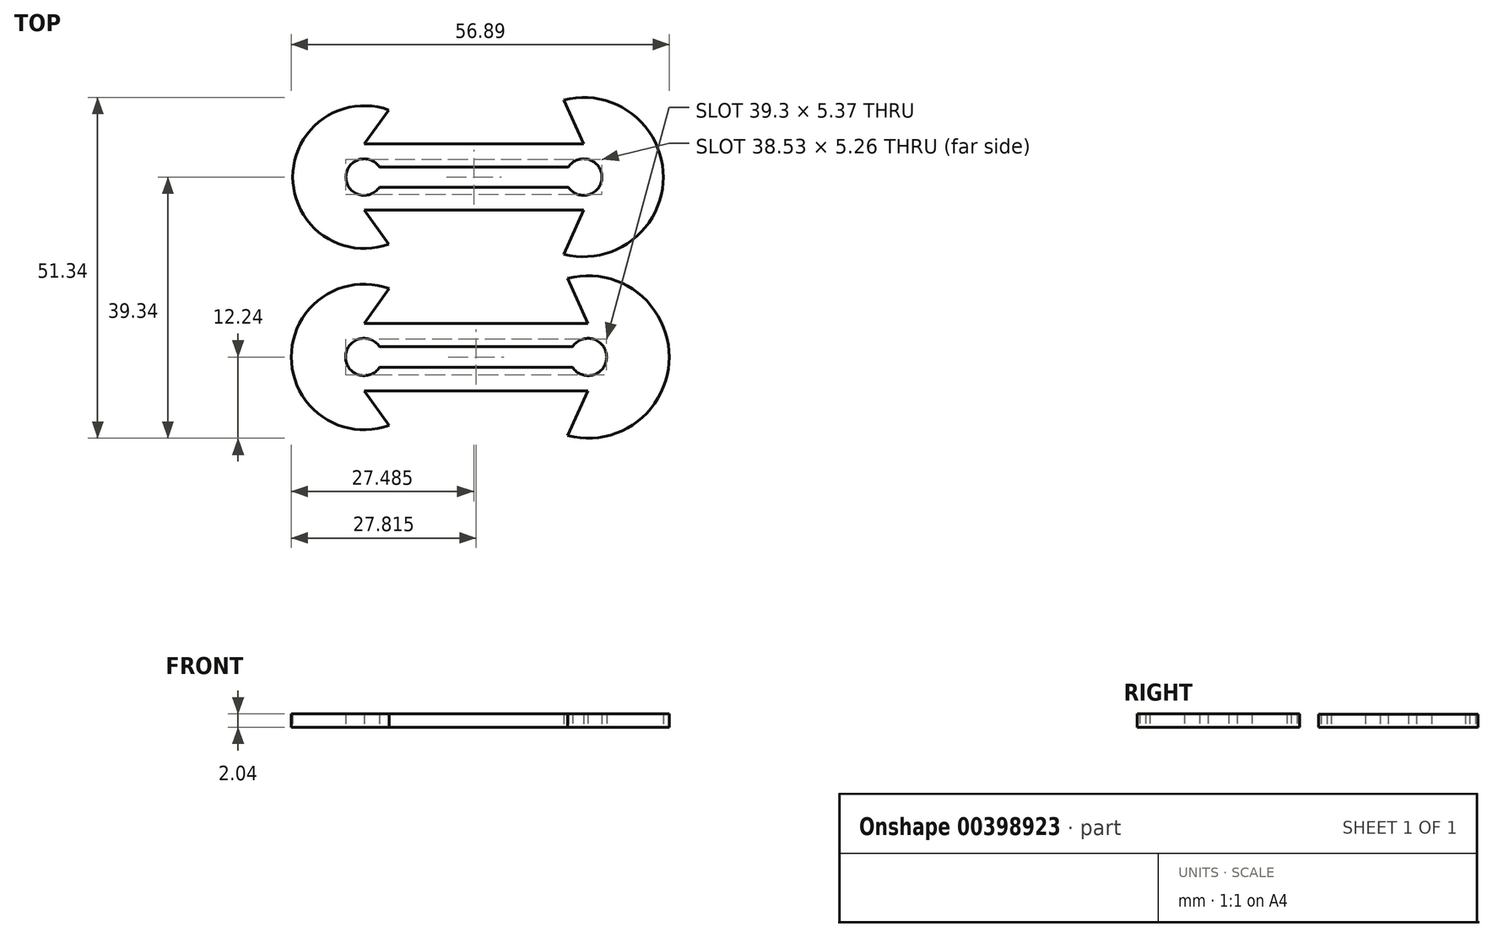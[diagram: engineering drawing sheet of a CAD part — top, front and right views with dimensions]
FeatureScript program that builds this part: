
annotation { "Feature Type Name" : "Feature", "Feature Type Description" : "" }
export const myFeature = defineFeature(function(context is Context, id is Id, definition is map)
    precondition{}
    {
        {
            var Q0;
            Q0=qCreatedBy(makeId("Top.planeOp"),FACE);
            var sketch = newSketch(context, id + "F0", { "sketchPlane" : qUnion([Q0])});
            skArc(sketch, "E0", {"start": v(3.68, 10.1) * mm, "mid": v(-10.75, 0) * mm, "end": v(3.68, -10.1) * mm});
            skArc(sketch, "E1", {"start": v(30.04, -11.62) * mm, "mid": v(45.02, 0) * mm, "end": v(30.04, 11.62) * mm});
            skPoint(sketch, "E2.orphan", {"position": v(0, 4.36) * mm});
            skLineSegment(sketch, "E3.top", {"start": v(0, 4.98) * mm, "end": v(33.02, 4.98) * mm});
            skPoint(sketch, "E4.orphan", {"position": v(0, 10.75) * mm});
            skLineSegment(sketch, "E5", {"start": v(3.68, 10.1) * mm, "end": v(0, 4.98) * mm});
            skLineSegment(sketch, "E6", {"start": v(3.68, -10.1) * mm, "end": v(0, -4.98) * mm});
            skPoint(sketch, "E7.orphan", {"position": v(30.04, -11.62) * mm});
            skLineSegment(sketch, "E8", {"start": v(30.04, 11.62) * mm, "end": v(33.02, 4.98) * mm});
            skLineSegment(sketch, "E9", {"start": v(30.04, -11.62) * mm, "end": v(33.02, -4.98) * mm});
            skPoint(sketch, "E10.orphan", {"position": v(33.02, 12) * mm});
            skLineSegment(sketch, "E11.bottom", {"start": v(0, 0) * mm, "end": v(33.03, 0) * mm});
            skLineSegment(sketch, "E11.top", {"start": v(0, -1.54) * mm, "end": v(33.03, -1.54) * mm});
            skLineSegment(sketch, "E11.left", {"start": v(0, 0) * mm, "end": v(0, -1.54) * mm});
            skLineSegment(sketch, "E11.right", {"start": v(33.03, 0) * mm, "end": v(33.03, -1.54) * mm});
            skLineSegment(sketch, "E12.MirrorCS", {"start": v(0, 1.54) * mm, "end": v(33.03, 1.54) * mm});
            skLineSegment(sketch, "E13.MirrorCS", {"start": v(0, 0) * mm, "end": v(0, 1.54) * mm});
            skLineSegment(sketch, "E14.MirrorCS", {"start": v(33.03, 0) * mm, "end": v(33.03, 1.54) * mm});
            skLineSegment(sketch, "E15.MirrorCS", {"start": v(0, -4.98) * mm, "end": v(33.02, -4.98) * mm});
            skSolve(sketch);
        }
        {
            var Q0;
            Q0=qSketchRegion(id+"F0",true);
            extrude(context, id + "F1", {"entities" : qUnion([Q0]), "depth" : 2 * mm});
        }
        {
            var Q0;
            Q0=sQuery(id+"F0.wireOp",VERTEX,"E11.bottom.start");
            var Q1;
            Q1=sQuery(id+"F0.wireOp",VERTEX,"E11.right.start");
            var Q2;
            Q2=makeQuery(id+"F1.opExtrude","SWEPT_BODY",BODY,{"disambiguationData":[OSD([sQuery(id+"F0.wireOp",EDGE,"E0"),sQuery(id+"F0.wireOp",EDGE,"E1"),sQuery(id+"F0.wireOp",EDGE,"E3.top"),sQuery(id+"F0.wireOp",EDGE,"09a4da2d-7d0f-4de4-b051-a0dd602dcae70.MirrorCS"),sQuery(id+"F0.wireOp",EDGE,"kJXo7HvB-q0wJ-KMkF-qbSK-HqD1jnp9HCBe"),sQuery(id+"F0.wireOp",EDGE,"2FfrFlms-cFN7-iBXT-GTBb-5V8th5hE76g1")])]});
            hole(context, id + "F2", {"style" : HoleStyle.SIMPLE, "endStyle" : HoleEndStyle.THROUGH, "oppositeDirection" : true, "standardTappedOrClearance" : lookupTablePath({ "standard" : "ISO", "fit" : "Normal", "size" : "M5", "type" : "Clearance" }), "standardBlindInLast" : lookupTablePath({ "fit" : "Standard", "standard" : "ISO", "size" : "M5", "type" : "Clearance" }), "holeDiameter" : 5.5 * mm, "isTappedThrough" : true, "tappedDepth" : 12 * mm, "tapClearance" : 3, "locations" : qUnion([Q0, Q1]), "scope" : qUnion([Q2])});
        }
        {
            var Q0;
            Q0=makeQuery(id+"F1.opExtrude","SWEPT_BODY",BODY,{"disambiguationData":[OSD([sQuery(id+"F0.wireOp",EDGE,"E0"),sQuery(id+"F0.wireOp",EDGE,"E1"),sQuery(id+"F0.wireOp",EDGE,"E3.top"),sQuery(id+"F0.wireOp",EDGE,"E5"),sQuery(id+"F0.wireOp",EDGE,"E6"),sQuery(id+"F0.wireOp",EDGE,"E8"),sQuery(id+"F0.wireOp",EDGE,"E9"),sQuery(id+"F0.wireOp",EDGE,"E11.top"),sQuery(id+"F0.wireOp",EDGE,"E11.left"),sQuery(id+"F0.wireOp",EDGE,"E11.right"),sQuery(id+"F0.wireOp",EDGE,"E12.MirrorCS"),sQuery(id+"F0.wireOp",EDGE,"E13.MirrorCS"),sQuery(id+"F0.wireOp",EDGE,"E14.MirrorCS"),sQuery(id+"F0.wireOp",EDGE,"E15.MirrorCS")])]});
            var Q1;
            Q1=sQuery(id+"F0.wireOp",VERTEX,"E6.end");
            transform(context, id + "F3", {"entities" : qUnion([Q0]), "transformType" : TransformType.SCALE_UNIFORMLY, "scale" : 1.02, "scalePoint" : qUnion([Q1]), "makeCopy" : true});
        }
        {
            var Q0;
            Q0=makeQuery(id+"F3.opPattern","COPY",BODY,{"derivedFrom":makeQuery(id+"F1.opExtrude","SWEPT_BODY",BODY,{"disambiguationData":[OSD([sQuery(id+"F0.wireOp",EDGE,"E0"),sQuery(id+"F0.wireOp",EDGE,"E1"),sQuery(id+"F0.wireOp",EDGE,"E3.top"),sQuery(id+"F0.wireOp",EDGE,"E5"),sQuery(id+"F0.wireOp",EDGE,"E6"),sQuery(id+"F0.wireOp",EDGE,"E8"),sQuery(id+"F0.wireOp",EDGE,"E9"),sQuery(id+"F0.wireOp",EDGE,"E11.top"),sQuery(id+"F0.wireOp",EDGE,"E11.left"),sQuery(id+"F0.wireOp",EDGE,"E11.right"),sQuery(id+"F0.wireOp",EDGE,"E12.MirrorCS"),sQuery(id+"F0.wireOp",EDGE,"E13.MirrorCS"),sQuery(id+"F0.wireOp",EDGE,"E14.MirrorCS"),sQuery(id+"F0.wireOp",EDGE,"E15.MirrorCS")])]}),"instanceName":"1"});
            transform(context, id + "F4", {"entities" : qUnion([Q0]), "transformType" : TransformType.TRANSLATION_3D, "dx" : 0 * mm, "dy" : -27.2 * mm, "dz" : 0 * mm, "makeCopy" : false});
        }
    });
